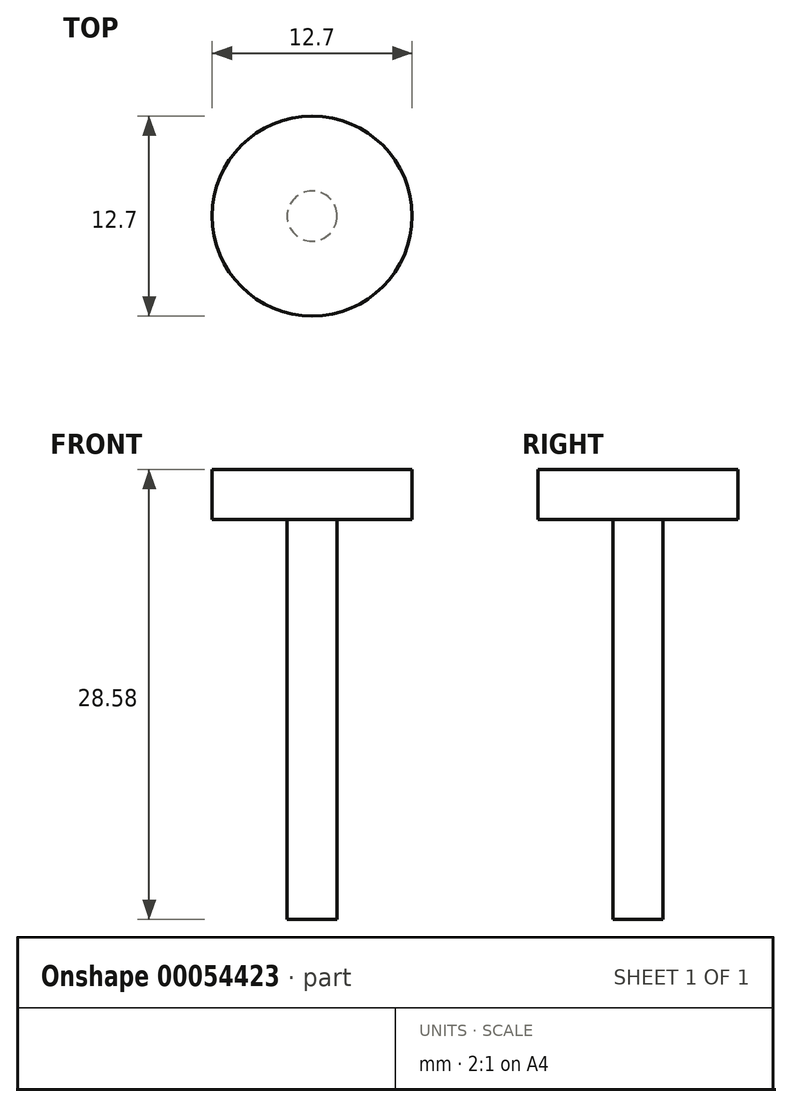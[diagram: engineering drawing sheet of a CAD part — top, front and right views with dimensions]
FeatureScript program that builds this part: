
annotation { "Feature Type Name" : "Feature", "Feature Type Description" : "" }
export const myFeature = defineFeature(function(context is Context, id is Id, definition is map)
    precondition{}
    {
        {
            var Q0;
            Q0=qCreatedBy(makeId("Top.planeOp"),FACE);
            var sketch = newSketch(context, id + "F0", { "sketchPlane" : qUnion([Q0])});
            skCircle(sketch, "E0", {"center": v(0, 0) * mm, "radius": 6.35 * mm});
            skSolve(sketch);
        }
        {
            var Q0;
            Q0=makeQuery(id+"F0.imprint","IMPRINT",FACE,{"disambiguationData":[TD([[makeQuery(id+"F0.imprint","IMPRINT",EDGE,{"derivedFrom":sQuery(id+"F0.wireOp",EDGE,"E0")}),1.0]])]});
            extrude(context, id + "F1", {"entities" : qUnion([Q0]), "depth" : 3.17 * mm});
        }
        {
            var Q0;
            Q0=makeQuery(id+"F1.opExtrude","CAP_FACE",FACE,{"disambiguationData":[OSD([sQuery(id+"F0.wireOp",EDGE,"E0")])],"isStart":true});
            var sketch = newSketch(context, id + "F2", { "sketchPlane" : qUnion([Q0])});
            skCircle(sketch, "E1", {"center": v(0, 0) * mm, "radius": 1.59 * mm});
            skSolve(sketch);
        }
        {
            var Q0;
            Q0=makeQuery(id+"F2.imprint","IMPRINT",FACE,{"disambiguationData":[TD([[makeQuery(id+"F2.imprint","IMPRINT",EDGE,{"derivedFrom":sQuery(id+"F2.wireOp",EDGE,"E1")}),1.0]])]});
            extrude(context, id + "F3", {"entities" : qUnion([Q0]), "operationType" : NewBodyOperationType.ADD, "depth" : 25.4 * mm});
        }
    });
